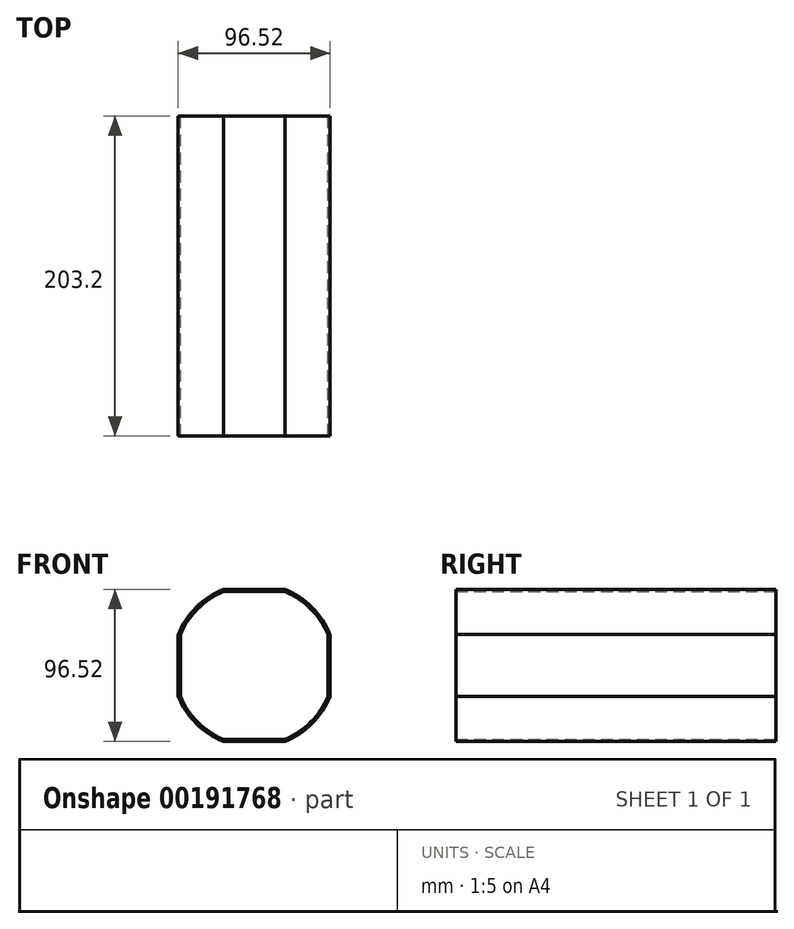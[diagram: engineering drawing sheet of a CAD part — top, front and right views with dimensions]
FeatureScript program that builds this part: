
annotation { "Feature Type Name" : "Feature", "Feature Type Description" : "" }
export const myFeature = defineFeature(function(context is Context, id is Id, definition is map)
    precondition{}
    {
        {
            var Q0;
            Q0=qCreatedBy(makeId("Front.planeOp"),FACE);
            var sketch = newSketch(context, id + "F0", { "sketchPlane" : qUnion([Q0])});
            skCircle(sketch, "E0", {"center": v(0, 0) * mm, "radius": 50.8 * mm});
            skCircle(sketch, "E1", {"center": v(0, 0) * mm, "radius": 52.07 * mm});
            skLineSegment(sketch, "E2", {"start": v(0, -48.26) * mm, "end": v(19.55, -48.26) * mm});
            skLineSegment(sketch, "E3", {"start": v(19.55, -48.26) * mm, "end": v(19.55, -46.89) * mm});
            skLineSegment(sketch, "E4", {"start": v(19.55, -46.89) * mm, "end": v(-19.55, -46.89) * mm});
            skLineSegment(sketch, "E5", {"start": v(-19.55, -46.89) * mm, "end": v(-19.55, -48.26) * mm});
            skLineSegment(sketch, "E6", {"start": v(-19.55, -48.26) * mm, "end": v(0, -48.26) * mm});
            skLineSegment(sketch, "E7", {"start": v(-48.26, 0) * mm, "end": v(-48.26, 19.55) * mm});
            skLineSegment(sketch, "E8", {"start": v(-48.26, 19.55) * mm, "end": v(-46.89, 19.55) * mm});
            skLineSegment(sketch, "E9", {"start": v(-46.89, 19.55) * mm, "end": v(-46.89, -19.55) * mm});
            skLineSegment(sketch, "E10", {"start": v(-46.89, -19.55) * mm, "end": v(-48.26, -19.55) * mm});
            skLineSegment(sketch, "E11", {"start": v(-48.26, -19.55) * mm, "end": v(-48.26, 0) * mm});
            skLineSegment(sketch, "E12", {"start": v(48.26, 0) * mm, "end": v(48.26, -19.55) * mm});
            skLineSegment(sketch, "E13", {"start": v(48.26, -19.55) * mm, "end": v(46.89, -19.55) * mm});
            skLineSegment(sketch, "E14", {"start": v(46.89, -19.55) * mm, "end": v(46.89, 19.55) * mm});
            skLineSegment(sketch, "E15", {"start": v(46.89, 19.55) * mm, "end": v(48.26, 19.55) * mm});
            skLineSegment(sketch, "E16", {"start": v(48.26, 19.55) * mm, "end": v(48.26, 0) * mm});
            skLineSegment(sketch, "E17", {"start": v(0, 48.26) * mm, "end": v(19.55, 48.26) * mm});
            skLineSegment(sketch, "E18", {"start": v(19.55, 48.26) * mm, "end": v(19.55, 46.89) * mm});
            skLineSegment(sketch, "E19", {"start": v(19.55, 46.89) * mm, "end": v(-19.55, 46.89) * mm});
            skLineSegment(sketch, "E20", {"start": v(-19.55, 46.89) * mm, "end": v(-19.55, 48.26) * mm});
            skLineSegment(sketch, "E21", {"start": v(-19.55, 48.26) * mm, "end": v(0, 48.26) * mm});
            skSolve(sketch);
        }
        {
            var Q0;
            {var subQ0=sQuery(id+"F0.wireOp",EDGE,"E8");Q0=makeQuery(id+"F0.imprint","IMPRINT",FACE,{"disambiguationData":[TD([[makeQuery(id+"F0.imprint","IMPRINT",EDGE,{"derivedFrom":subQ0}),1.0]])]});}
            var Q1;
            {var subQ0=sQuery(id+"F0.wireOp",EDGE,"E15");Q1=makeQuery(id+"F0.imprint","IMPRINT",FACE,{"disambiguationData":[TD([[makeQuery(id+"F0.imprint","IMPRINT",EDGE,{"derivedFrom":subQ0}),1.0]])]});}
            var Q2;
            {var subQ0=sQuery(id+"F0.wireOp",EDGE,"E3");Q2=makeQuery(id+"F0.imprint","IMPRINT",FACE,{"disambiguationData":[TD([[makeQuery(id+"F0.imprint","IMPRINT",EDGE,{"derivedFrom":subQ0}),-1.0]])]});}
            var Q3;
            {var subQ0=sQuery(id+"F0.wireOp",EDGE,"E5");Q3=makeQuery(id+"F0.imprint","IMPRINT",FACE,{"disambiguationData":[TD([[makeQuery(id+"F0.imprint","IMPRINT",EDGE,{"derivedFrom":subQ0}),-1.0]])]});}
            extrude(context, id + "F1", {"entities" : qUnion([Q0, Q1, Q2, Q3]), "depth" : 203.2 * mm});
        }
        {
            var Q0;
            {var subQ0=sQuery(id+"F0.wireOp",EDGE,"E10");Q0=makeQuery(id+"F0.imprint","IMPRINT",FACE,{"disambiguationData":[TD([[makeQuery(id+"F0.imprint","IMPRINT",EDGE,{"derivedFrom":subQ0}),-1.0]])]});}
            var Q1;
            {var subQ5=sQuery(id+"F0.wireOp",EDGE,"E9");Q1=makeQuery(id+"F0.imprint","IMPRINT",FACE,{"disambiguationData":[TD([[makeQuery(id+"F0.imprint","IMPRINT",EDGE,{"derivedFrom":subQ5}),-1.0]])]});}
            var Q2;
            {var subQ0=sQuery(id+"F0.wireOp",EDGE,"E8");Q2=makeQuery(id+"F0.imprint","IMPRINT",FACE,{"disambiguationData":[TD([[makeQuery(id+"F0.imprint","IMPRINT",EDGE,{"derivedFrom":subQ0}),-1.0]])]});}
            var Q3;
            {var subQ0=sQuery(id+"F0.wireOp",EDGE,"E20");Q3=makeQuery(id+"F0.imprint","IMPRINT",FACE,{"disambiguationData":[TD([[makeQuery(id+"F0.imprint","IMPRINT",EDGE,{"derivedFrom":subQ0}),-1.0]])]});}
            var Q4;
            {var subQ5=sQuery(id+"F0.wireOp",EDGE,"E19");Q4=makeQuery(id+"F0.imprint","IMPRINT",FACE,{"disambiguationData":[TD([[makeQuery(id+"F0.imprint","IMPRINT",EDGE,{"derivedFrom":subQ5}),-1.0]])]});}
            var Q5;
            {var subQ0=sQuery(id+"F0.wireOp",EDGE,"E18");Q5=makeQuery(id+"F0.imprint","IMPRINT",FACE,{"disambiguationData":[TD([[makeQuery(id+"F0.imprint","IMPRINT",EDGE,{"derivedFrom":subQ0}),-1.0]])]});}
            var Q6;
            {var subQ0=sQuery(id+"F0.wireOp",EDGE,"E15");Q6=makeQuery(id+"F0.imprint","IMPRINT",FACE,{"disambiguationData":[TD([[makeQuery(id+"F0.imprint","IMPRINT",EDGE,{"derivedFrom":subQ0}),-1.0]])]});}
            var Q7;
            {var subQ0=sQuery(id+"F0.wireOp",EDGE,"E14");Q7=makeQuery(id+"F0.imprint","IMPRINT",FACE,{"disambiguationData":[TD([[makeQuery(id+"F0.imprint","IMPRINT",EDGE,{"derivedFrom":subQ0}),-1.0]])]});}
            var Q8;
            {var subQ0=sQuery(id+"F0.wireOp",EDGE,"E13");Q8=makeQuery(id+"F0.imprint","IMPRINT",FACE,{"disambiguationData":[TD([[makeQuery(id+"F0.imprint","IMPRINT",EDGE,{"derivedFrom":subQ0}),-1.0]])]});}
            var Q9;
            {var subQ0=sQuery(id+"F0.wireOp",EDGE,"E4");Q9=makeQuery(id+"F0.imprint","IMPRINT",FACE,{"disambiguationData":[TD([[makeQuery(id+"F0.imprint","IMPRINT",EDGE,{"derivedFrom":subQ0}),1.0]])]});}
            var Q10;
            {var subQ0=sQuery(id+"F0.wireOp",EDGE,"E3");Q10=makeQuery(id+"F0.imprint","IMPRINT",FACE,{"disambiguationData":[TD([[makeQuery(id+"F0.imprint","IMPRINT",EDGE,{"derivedFrom":subQ0}),1.0]])]});}
            var Q11;
            {var subQ0=sQuery(id+"F0.wireOp",EDGE,"E5");Q11=makeQuery(id+"F0.imprint","IMPRINT",FACE,{"disambiguationData":[TD([[makeQuery(id+"F0.imprint","IMPRINT",EDGE,{"derivedFrom":subQ0}),1.0]])]});}
            extrude(context, id + "F2", {"entities" : qUnion([Q0, Q1, Q2, Q3, Q4, Q5, Q6, Q7, Q8, Q9, Q10, Q11]), "depth" : 203.2 * mm});
        }
    });
